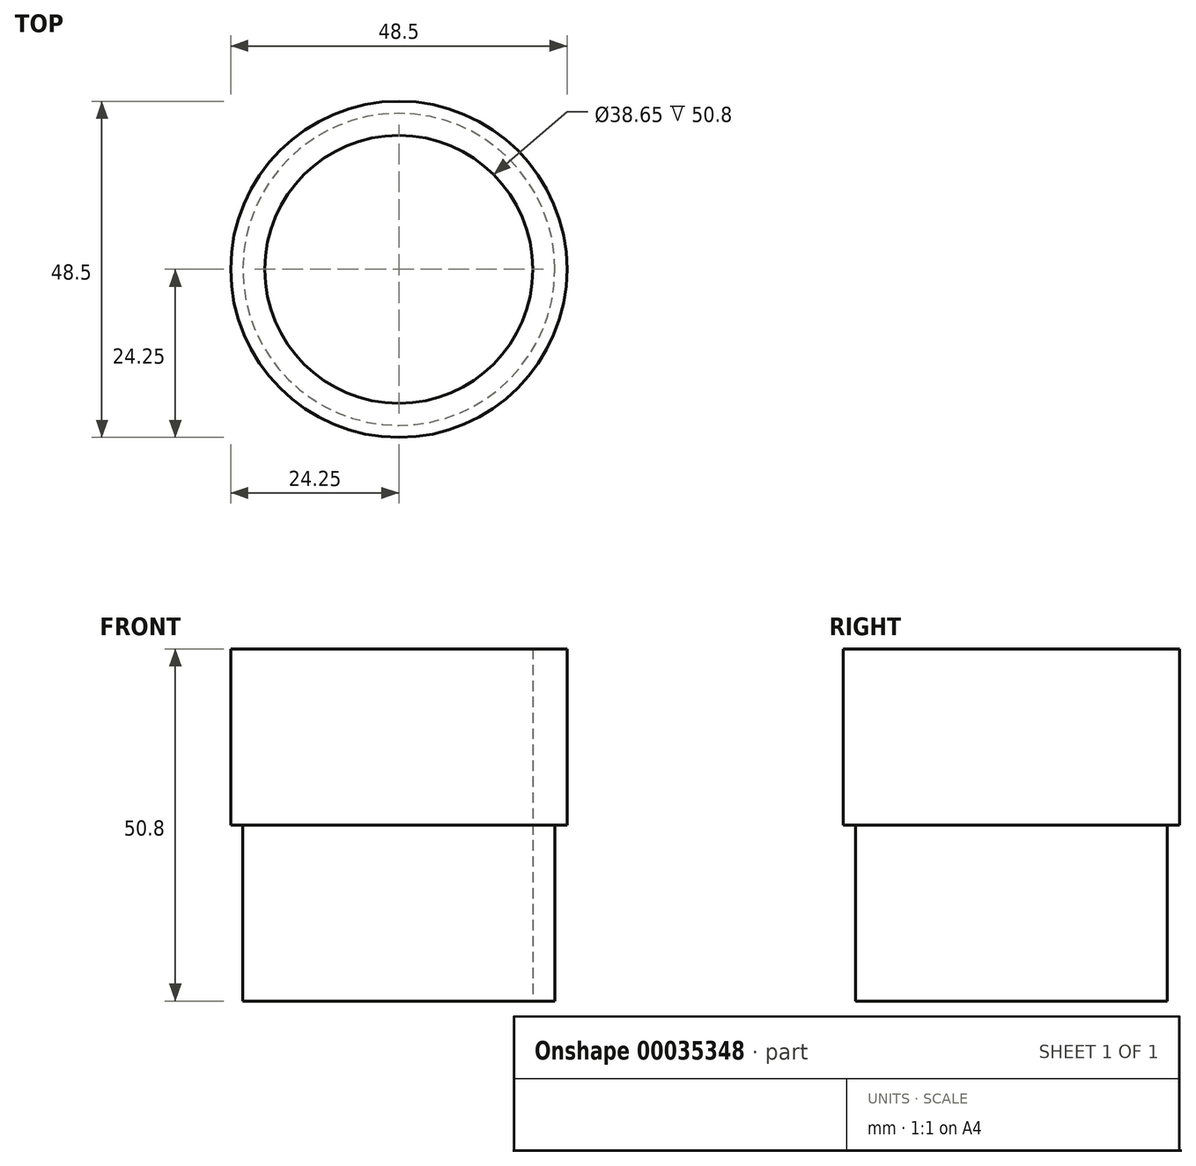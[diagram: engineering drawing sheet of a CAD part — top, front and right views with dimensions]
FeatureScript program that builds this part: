
annotation { "Feature Type Name" : "Feature", "Feature Type Description" : "" }
export const myFeature = defineFeature(function(context is Context, id is Id, definition is map)
    precondition{}
    {
        {
            var Q0;
            Q0=qCreatedBy(makeId("Top.planeOp"),FACE);
            var sketch = newSketch(context, id + "F0", { "sketchPlane" : qUnion([Q0])});
            skCircle(sketch, "E0", {"center": v(0, 0) * mm, "radius": 22.5 * mm});
            skCircle(sketch, "E1.0", {"center": v(0, 0) * mm, "radius": 19.32 * mm});
            skSolve(sketch);
        }
        {
            var Q0;
            Q0=makeQuery(id+"F0.imprint","IMPRINT",FACE,{"disambiguationData":[TD([[makeQuery(id+"F0.imprint","IMPRINT",EDGE,{"derivedFrom":sQuery(id+"F0.wireOp",EDGE,"E0")}),1.0]])]});
            extrude(context, id + "F1", {"entities" : qUnion([Q0]), "depth" : 25.4 * mm});
        }
        {
            var Q0;
            Q0=makeQuery(id+"F1.opExtrude","CAP_FACE",FACE,{"disambiguationData":[OSD([sQuery(id+"F0.wireOp",EDGE,"E0"),sQuery(id+"F0.wireOp",EDGE,"E1.0")])],"isStart":false});
            var sketch = newSketch(context, id + "F2", { "sketchPlane" : qUnion([Q0])});
            skCircle(sketch, "E2.0", {"center": v(0, 0) * mm, "radius": 24.25 * mm});
            skCircle(sketch, "E3.0", {"center": v(0, 0) * mm, "radius": 19.32 * mm});
            skSolve(sketch);
        }
        {
            var Q0;
            Q0=makeQuery(id+"F2.imprint","IMPRINT",FACE,{"disambiguationData":[TD([[makeQuery(id+"F2.imprint","IMPRINT",EDGE,{"derivedFrom":sQuery(id+"F2.wireOp",EDGE,"E2.0")}),1.0]])]});
            var Q1;
            Q1=makeQuery(id+"F2.imprint","IMPRINT",FACE,{"disambiguationData":[TD([[makeQuery(id+"F2.imprint","IMPRINT",EDGE,{"derivedFrom":sQuery(id+"F2.wireOp",EDGE,"E3.0")}),-1.0]])]});
            extrude(context, id + "F3", {"entities" : qUnion([Q0, Q1]), "operationType" : NewBodyOperationType.ADD, "depth" : 25.4 * mm});
        }
    });
